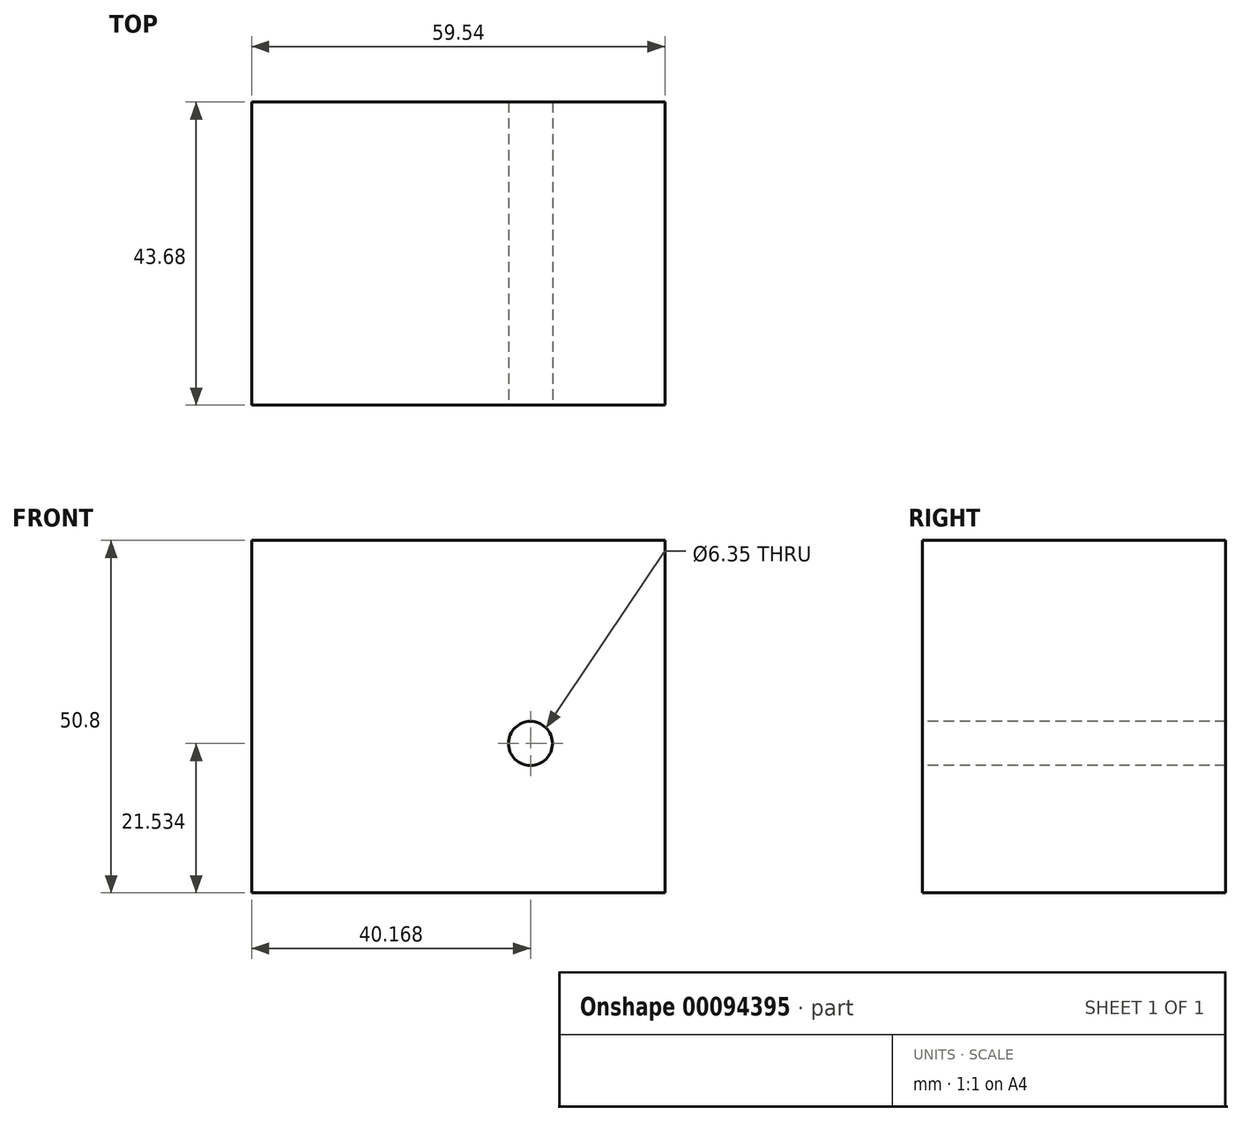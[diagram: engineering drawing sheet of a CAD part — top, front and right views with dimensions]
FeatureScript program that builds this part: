
annotation { "Feature Type Name" : "Feature", "Feature Type Description" : "" }
export const myFeature = defineFeature(function(context is Context, id is Id, definition is map)
    precondition{}
    {
        {
            var Q0;
            Q0=qCreatedBy(makeId("Top.planeOp"),FACE);
            var sketch = newSketch(context, id + "F0", { "sketchPlane" : qUnion([Q0])});
            skLineSegment(sketch, "E0.bottom", {"start": v(0, 0) * mm, "end": v(59.54, 0) * mm});
            skLineSegment(sketch, "E0.top", {"start": v(0, -43.68) * mm, "end": v(59.54, -43.68) * mm});
            skLineSegment(sketch, "E0.left", {"start": v(0, 0) * mm, "end": v(0, -43.68) * mm});
            skLineSegment(sketch, "E0.right", {"start": v(59.54, 0) * mm, "end": v(59.54, -43.68) * mm});
            skSolve(sketch);
        }
        {
            var Q0;
            Q0 = qSketchRegion(id + "F0", true);
            extrude(context, id + "F1", {"entities" : qUnion([Q0]), "depth" : 50.8 * mm});
        }
        {
            var Q0;
            Q0=makeQuery(id+"F1.opExtrude","SWEPT_FACE",FACE,{"disambiguationData":[OSD([sQuery(id+"F0.wireOp",EDGE,"E0.top")])]});
            var sketch = newSketch(context, id + "F2", { "sketchPlane" : qUnion([Q0])});
            skCircle(sketch, "E1", {"center": v(40.17, 21.53) * mm, "radius": 6.96 * mm});
            skSolve(sketch);
        }
        {
            var Q0;
            Q0=sQuery(id+"F2.wireOp",VERTEX,"E1.center");
            var Q1;
            Q1=makeQuery(id+"F1.opExtrude","SWEPT_BODY",BODY,{"disambiguationData":[OSD([sQuery(id+"F0.wireOp",EDGE,"E0.bottom"),sQuery(id+"F0.wireOp",EDGE,"E0.top"),sQuery(id+"F0.wireOp",EDGE,"E0.left"),sQuery(id+"F0.wireOp",EDGE,"E0.right")])]});
            hole(context, id + "F3", {"style" : HoleStyle.SIMPLE, "endStyle" : HoleEndStyle.THROUGH, "holeDiameter" : 6.35 * mm, "locations" : qUnion([Q0]), "scope" : qUnion([Q1]), "isTappedThrough" : true});
        }
    });
